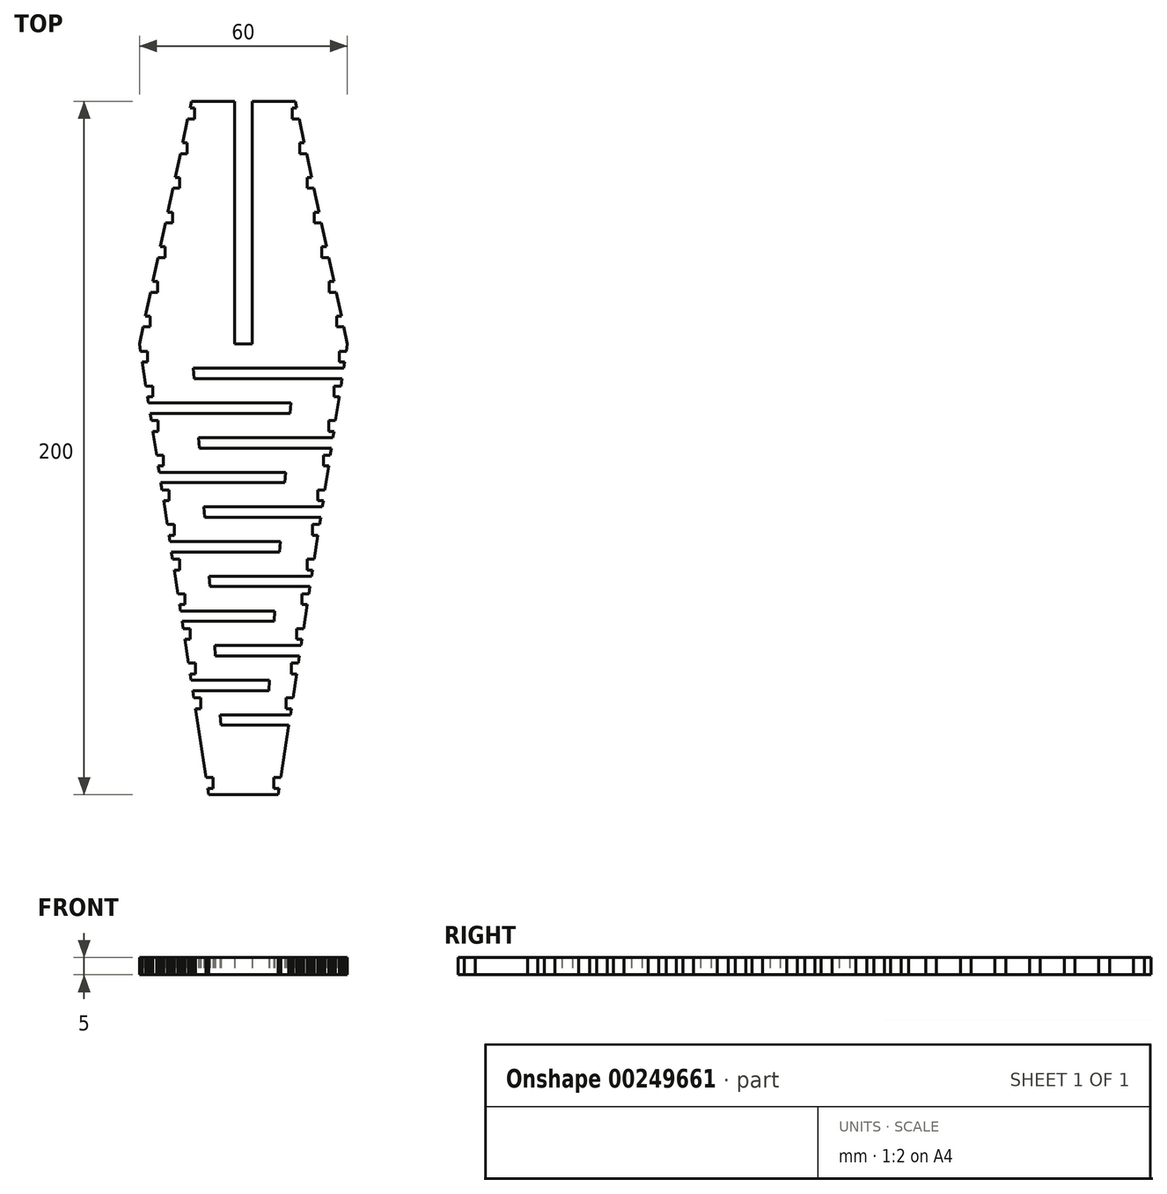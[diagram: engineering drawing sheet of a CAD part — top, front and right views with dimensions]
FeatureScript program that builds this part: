
annotation { "Feature Type Name" : "Feature", "Feature Type Description" : "" }
export const myFeature = defineFeature(function(context is Context, id is Id, definition is map)
    precondition{}
    {
        {
            var Q0;
            Q0=qCreatedBy(makeId("Top.planeOp"),FACE);
            var sketch = newSketch(context, id + "F0", { "sketchPlane" : qUnion([Q0])});
            skLineSegment(sketch, "E0", {"start": v(-15, 100) * mm, "end": v(-2.5, 100) * mm});
            skLineSegment(sketch, "E1", {"start": v(2.5, 100) * mm, "end": v(15, 100) * mm});
            skLineSegment(sketch, "E2", {"start": v(15, 100) * mm, "end": v(15.42, 98.05) * mm});
            skLineSegment(sketch, "E3", {"start": v(16.08, 94.95) * mm, "end": v(17.56, 88.05) * mm});
            skLineSegment(sketch, "E4", {"start": v(18.22, 84.95) * mm, "end": v(19.7, 78.05) * mm});
            skLineSegment(sketch, "E5", {"start": v(20.37, 74.95) * mm, "end": v(21.85, 68.05) * mm});
            skLineSegment(sketch, "E6", {"start": v(22.51, 64.95) * mm, "end": v(23.99, 58.05) * mm});
            skLineSegment(sketch, "E7", {"start": v(24.65, 54.95) * mm, "end": v(26.13, 48.05) * mm});
            skLineSegment(sketch, "E8", {"start": v(26.8, 44.95) * mm, "end": v(28.28, 38.05) * mm});
            skLineSegment(sketch, "E9", {"start": v(28.94, 34.95) * mm, "end": v(30, 30) * mm});
            skLineSegment(sketch, "E10", {"start": v(-15, 100) * mm, "end": v(-15.42, 98.05) * mm});
            skLineSegment(sketch, "E11", {"start": v(-16.08, 94.95) * mm, "end": v(-17.56, 88.05) * mm});
            skLineSegment(sketch, "E12", {"start": v(-18.22, 84.95) * mm, "end": v(-19.7, 78.05) * mm});
            skLineSegment(sketch, "E13", {"start": v(-20.37, 74.95) * mm, "end": v(-21.85, 68.05) * mm});
            skLineSegment(sketch, "E14", {"start": v(-22.51, 64.95) * mm, "end": v(-23.99, 58.05) * mm});
            skLineSegment(sketch, "E15", {"start": v(-24.65, 54.95) * mm, "end": v(-26.13, 48.05) * mm});
            skLineSegment(sketch, "E16", {"start": v(-26.8, 44.95) * mm, "end": v(-28.28, 38.05) * mm});
            skLineSegment(sketch, "E17", {"start": v(-28.94, 34.95) * mm, "end": v(-30, 30) * mm});
            skLineSegment(sketch, "E18", {"start": v(0, -100) * mm, "end": v(10, -100) * mm});
            skLineSegment(sketch, "E19", {"start": v(10, -100) * mm, "end": v(10.28, -98.2) * mm});
            skLineSegment(sketch, "E20", {"start": v(10.76, -95.1) * mm, "end": v(13.08, -80) * mm});
            skLineSegment(sketch, "E21", {"start": v(13.54, -77) * mm, "end": v(13.82, -75.2) * mm});
            skLineSegment(sketch, "E22", {"start": v(14.3, -72.1) * mm, "end": v(15.36, -65.2) * mm});
            skLineSegment(sketch, "E23", {"start": v(15.83, -62.1) * mm, "end": v(16.15, -60) * mm});
            skLineSegment(sketch, "E24", {"start": v(16.62, -57) * mm, "end": v(16.9, -55.2) * mm});
            skLineSegment(sketch, "E25", {"start": v(17.37, -52.1) * mm, "end": v(18.43, -45.2) * mm});
            skLineSegment(sketch, "E26", {"start": v(18.9, -42.1) * mm, "end": v(19.23, -40) * mm});
            skLineSegment(sketch, "E27", {"start": v(19.7, -37) * mm, "end": v(19.97, -35.2) * mm});
            skLineSegment(sketch, "E28", {"start": v(20.45, -32.1) * mm, "end": v(21.5, -25.2) * mm});
            skLineSegment(sketch, "E29", {"start": v(21.99, -22.1) * mm, "end": v(22.3, -20) * mm});
            skLineSegment(sketch, "E30", {"start": v(22.77, -17) * mm, "end": v(23.05, -15.2) * mm});
            skLineSegment(sketch, "E31", {"start": v(23.52, -12.1) * mm, "end": v(24.59, -5.2) * mm});
            skLineSegment(sketch, "E32", {"start": v(25.06, -2.1) * mm, "end": v(25.38, 0) * mm});
            skLineSegment(sketch, "E33", {"start": v(25.85, 3) * mm, "end": v(26.12, 4.8) * mm});
            skLineSegment(sketch, "E34", {"start": v(26.6, 7.9) * mm, "end": v(27.66, 14.8) * mm});
            skLineSegment(sketch, "E35", {"start": v(28.14, 17.9) * mm, "end": v(28.46, 20) * mm});
            skLineSegment(sketch, "E36", {"start": v(28.92, 23) * mm, "end": v(29.2, 24.8) * mm});
            skLineSegment(sketch, "E37", {"start": v(29.68, 27.9) * mm, "end": v(30, 30) * mm});
            skLineSegment(sketch, "E38", {"start": v(0, -100) * mm, "end": v(-10, -100) * mm});
            skLineSegment(sketch, "E39", {"start": v(-10, -100) * mm, "end": v(-10.28, -98.2) * mm});
            skLineSegment(sketch, "E40", {"start": v(-10.76, -95.1) * mm, "end": v(-13.82, -75.2) * mm});
            skLineSegment(sketch, "E41", {"start": v(-14.3, -72.1) * mm, "end": v(-14.62, -70) * mm});
            skLineSegment(sketch, "E42", {"start": v(-15.08, -67) * mm, "end": v(-15.36, -65.2) * mm});
            skLineSegment(sketch, "E43", {"start": v(-15.83, -62.1) * mm, "end": v(-16.9, -55.2) * mm});
            skLineSegment(sketch, "E44", {"start": v(-17.37, -52.1) * mm, "end": v(-17.7, -50) * mm});
            skLineSegment(sketch, "E45", {"start": v(-18.15, -47) * mm, "end": v(-18.43, -45.2) * mm});
            skLineSegment(sketch, "E46", {"start": v(-18.9, -42.1) * mm, "end": v(-19.97, -35.2) * mm});
            skLineSegment(sketch, "E47", {"start": v(-20.45, -32.1) * mm, "end": v(-20.77, -30) * mm});
            skLineSegment(sketch, "E48", {"start": v(-21.23, -27) * mm, "end": v(-21.5, -25.2) * mm});
            skLineSegment(sketch, "E49", {"start": v(-21.99, -22.1) * mm, "end": v(-23.05, -15.2) * mm});
            skLineSegment(sketch, "E50", {"start": v(-23.52, -12.1) * mm, "end": v(-23.85, -10) * mm});
            skLineSegment(sketch, "E51", {"start": v(-24.3, -7) * mm, "end": v(-24.59, -5.2) * mm});
            skLineSegment(sketch, "E52", {"start": v(-25.06, -2.1) * mm, "end": v(-26.12, 4.8) * mm});
            skLineSegment(sketch, "E53", {"start": v(-26.6, 7.9) * mm, "end": v(-26.92, 10) * mm});
            skLineSegment(sketch, "E54", {"start": v(-27.38, 13) * mm, "end": v(-27.66, 14.8) * mm});
            skLineSegment(sketch, "E55", {"start": v(-28.14, 17.9) * mm, "end": v(-29.2, 24.8) * mm});
            skLineSegment(sketch, "E56", {"start": v(-29.68, 27.9) * mm, "end": v(-30, 30) * mm});
            skLineSegment(sketch, "E57", {"start": v(-14.46, 23) * mm, "end": v(28.92, 23) * mm});
            skLineSegment(sketch, "E58", {"start": v(-14.23, 20) * mm, "end": v(28.46, 20) * mm});
            skLineSegment(sketch, "E59", {"start": v(-27.38, 13) * mm, "end": v(13.7, 13) * mm});
            skLineSegment(sketch, "E60", {"start": v(-26.92, 10) * mm, "end": v(13.46, 10) * mm});
            skLineSegment(sketch, "E61", {"start": v(-12.92, 3) * mm, "end": v(25.85, 3) * mm});
            skLineSegment(sketch, "E62", {"start": v(-12.7, 0) * mm, "end": v(25.38, 0) * mm});
            skLineSegment(sketch, "E63", {"start": v(-24.3, -7) * mm, "end": v(12.15, -7) * mm});
            skLineSegment(sketch, "E64", {"start": v(-23.85, -10) * mm, "end": v(11.92, -10) * mm});
            skLineSegment(sketch, "E65", {"start": v(-11.38, -17) * mm, "end": v(22.77, -17) * mm});
            skLineSegment(sketch, "E66", {"start": v(-11.15, -20) * mm, "end": v(22.3, -20) * mm});
            skLineSegment(sketch, "E67", {"start": v(-21.23, -27) * mm, "end": v(10.62, -27) * mm});
            skLineSegment(sketch, "E68", {"start": v(-20.77, -30) * mm, "end": v(10.38, -30) * mm});
            skLineSegment(sketch, "E69", {"start": v(-9.85, -37) * mm, "end": v(19.7, -37) * mm});
            skLineSegment(sketch, "E70", {"start": v(-9.62, -40) * mm, "end": v(19.23, -40) * mm});
            skLineSegment(sketch, "E71", {"start": v(-18.15, -47) * mm, "end": v(9.08, -47) * mm});
            skLineSegment(sketch, "E72", {"start": v(-17.7, -50) * mm, "end": v(8.85, -50) * mm});
            skLineSegment(sketch, "E73", {"start": v(-8.3, -57) * mm, "end": v(16.62, -57) * mm});
            skLineSegment(sketch, "E74", {"start": v(-8.08, -60) * mm, "end": v(16.15, -60) * mm});
            skLineSegment(sketch, "E75", {"start": v(-15.08, -67) * mm, "end": v(7.54, -67) * mm});
            skLineSegment(sketch, "E76", {"start": v(-14.62, -70) * mm, "end": v(7.3, -70) * mm});
            skLineSegment(sketch, "E77", {"start": v(-6.77, -77) * mm, "end": v(13.54, -77) * mm});
            skLineSegment(sketch, "E78", {"start": v(-6.54, -80) * mm, "end": v(13.08, -80) * mm});
            skLineSegment(sketch, "E79", {"start": v(-12.92, 3) * mm, "end": v(-12.7, 0) * mm});
            skLineSegment(sketch, "E80", {"start": v(-11.38, -17) * mm, "end": v(-11.15, -20) * mm});
            skLineSegment(sketch, "E81", {"start": v(-9.85, -37) * mm, "end": v(-9.62, -40) * mm});
            skLineSegment(sketch, "E82", {"start": v(-8.3, -57) * mm, "end": v(-8.08, -60) * mm});
            skLineSegment(sketch, "E83", {"start": v(-6.77, -77) * mm, "end": v(-6.54, -80) * mm});
            skLineSegment(sketch, "E84", {"start": v(7.54, -67) * mm, "end": v(7.3, -70) * mm});
            skLineSegment(sketch, "E85", {"start": v(9.08, -47) * mm, "end": v(8.85, -50) * mm});
            skLineSegment(sketch, "E86", {"start": v(13.7, 13) * mm, "end": v(13.46, 10) * mm});
            skLineSegment(sketch, "E87", {"start": v(12.15, -7) * mm, "end": v(11.92, -10) * mm});
            skLineSegment(sketch, "E88", {"start": v(10.62, -27) * mm, "end": v(10.38, -30) * mm});
            skLineSegment(sketch, "E89", {"start": v(-26.94, 34.95) * mm, "end": v(-26.94, 38.05) * mm});
            skLineSegment(sketch, "E90", {"start": v(-14.08, 94.95) * mm, "end": v(-14.08, 98.05) * mm});
            skLineSegment(sketch, "E91", {"start": v(-2.5, 100) * mm, "end": v(-2.5, 30) * mm});
            skLineSegment(sketch, "E92", {"start": v(-2.5, 30) * mm, "end": v(2.5, 30) * mm});
            skLineSegment(sketch, "E93", {"start": v(2.5, 30) * mm, "end": v(2.5, 100) * mm});
            skLineSegment(sketch, "E94", {"start": v(-15.42, 98.05) * mm, "end": v(-14.08, 98.05) * mm});
            skLineSegment(sketch, "E95", {"start": v(-16.08, 94.95) * mm, "end": v(-14.08, 94.95) * mm});
            skLineSegment(sketch, "E96", {"start": v(-17.56, 88.05) * mm, "end": v(-16.22, 88.05) * mm});
            skLineSegment(sketch, "E97", {"start": v(-18.22, 84.95) * mm, "end": v(-16.22, 84.95) * mm});
            skLineSegment(sketch, "E98", {"start": v(-19.7, 78.05) * mm, "end": v(-18.37, 78.05) * mm});
            skLineSegment(sketch, "E99", {"start": v(-20.37, 74.95) * mm, "end": v(-18.37, 74.95) * mm});
            skLineSegment(sketch, "E100", {"start": v(-21.85, 68.05) * mm, "end": v(-20.51, 68.05) * mm});
            skLineSegment(sketch, "E101", {"start": v(-22.51, 64.95) * mm, "end": v(-20.51, 64.95) * mm});
            skLineSegment(sketch, "E102", {"start": v(-23.99, 58.05) * mm, "end": v(-22.65, 58.05) * mm});
            skLineSegment(sketch, "E103", {"start": v(-24.65, 54.95) * mm, "end": v(-22.65, 54.95) * mm});
            skLineSegment(sketch, "E104", {"start": v(-26.13, 48.05) * mm, "end": v(-24.8, 48.05) * mm});
            skLineSegment(sketch, "E105", {"start": v(-26.8, 44.95) * mm, "end": v(-24.8, 44.95) * mm});
            skLineSegment(sketch, "E106", {"start": v(-28.28, 38.05) * mm, "end": v(-26.94, 38.05) * mm});
            skLineSegment(sketch, "E107", {"start": v(-28.94, 34.95) * mm, "end": v(-26.94, 34.95) * mm});
            skLineSegment(sketch, "E108", {"start": v(-24.8, 44.95) * mm, "end": v(-24.8, 48.05) * mm});
            skLineSegment(sketch, "E109", {"start": v(-22.65, 54.95) * mm, "end": v(-22.65, 58.05) * mm});
            skLineSegment(sketch, "E110", {"start": v(-20.51, 64.95) * mm, "end": v(-20.51, 68.05) * mm});
            skLineSegment(sketch, "E111", {"start": v(-18.37, 74.95) * mm, "end": v(-18.37, 78.05) * mm});
            skLineSegment(sketch, "E112", {"start": v(-16.22, 84.95) * mm, "end": v(-16.22, 88.05) * mm});
            skLineSegment(sketch, "E113", {"start": v(-14.23, 20) * mm, "end": v(-14.46, 23) * mm});
            skLineSegment(sketch, "E114", {"start": v(-27.68, 27.9) * mm, "end": v(-27.68, 24.8) * mm});
            skLineSegment(sketch, "E115", {"start": v(-26.14, 17.9) * mm, "end": v(-26.14, 14.8) * mm});
            skLineSegment(sketch, "E116", {"start": v(-29.68, 27.9) * mm, "end": v(-27.68, 27.9) * mm});
            skLineSegment(sketch, "E117", {"start": v(-29.2, 24.8) * mm, "end": v(-27.68, 24.8) * mm});
            skLineSegment(sketch, "E118", {"start": v(-28.14, 17.9) * mm, "end": v(-26.14, 17.9) * mm});
            skLineSegment(sketch, "E119", {"start": v(-27.66, 14.8) * mm, "end": v(-26.14, 14.8) * mm});
            skLineSegment(sketch, "E120", {"start": v(-15.83, -62.1) * mm, "end": v(-13.83, -62.1) * mm});
            skLineSegment(sketch, "E121", {"start": v(-15.36, -65.2) * mm, "end": v(-13.83, -65.2) * mm});
            skLineSegment(sketch, "E122", {"start": v(-14.3, -72.1) * mm, "end": v(-12.3, -72.1) * mm});
            skLineSegment(sketch, "E123", {"start": v(-13.82, -75.2) * mm, "end": v(-12.3, -75.2) * mm});
            skLineSegment(sketch, "E124", {"start": v(-10.76, -95.1) * mm, "end": v(-8.76, -95.1) * mm});
            skLineSegment(sketch, "E125", {"start": v(-10.28, -98.2) * mm, "end": v(-8.76, -98.2) * mm});
            skLineSegment(sketch, "E126", {"start": v(-8.76, -95.1) * mm, "end": v(-8.76, -98.2) * mm});
            skLineSegment(sketch, "E127", {"start": v(-12.3, -72.1) * mm, "end": v(-12.3, -75.2) * mm});
            skLineSegment(sketch, "E128", {"start": v(-13.83, -62.1) * mm, "end": v(-13.83, -65.2) * mm});
            skLineSegment(sketch, "E129", {"start": v(-17.37, -52.1) * mm, "end": v(-15.37, -52.1) * mm});
            skLineSegment(sketch, "E130", {"start": v(-16.9, -55.2) * mm, "end": v(-15.37, -55.2) * mm});
            skLineSegment(sketch, "E131", {"start": v(-18.9, -42.1) * mm, "end": v(-16.9, -42.1) * mm});
            skLineSegment(sketch, "E132", {"start": v(-18.43, -45.2) * mm, "end": v(-16.9, -45.2) * mm});
            skLineSegment(sketch, "E133", {"start": v(-20.45, -32.1) * mm, "end": v(-18.45, -32.1) * mm});
            skLineSegment(sketch, "E134", {"start": v(-19.97, -35.2) * mm, "end": v(-18.45, -35.2) * mm});
            skLineSegment(sketch, "E135", {"start": v(-21.99, -22.1) * mm, "end": v(-19.99, -22.1) * mm});
            skLineSegment(sketch, "E136", {"start": v(-21.5, -25.2) * mm, "end": v(-19.99, -25.2) * mm});
            skLineSegment(sketch, "E137", {"start": v(-23.52, -12.1) * mm, "end": v(-21.52, -12.1) * mm});
            skLineSegment(sketch, "E138", {"start": v(-23.05, -15.2) * mm, "end": v(-21.52, -15.2) * mm});
            skLineSegment(sketch, "E139", {"start": v(-25.06, -2.1) * mm, "end": v(-23.06, -2.1) * mm});
            skLineSegment(sketch, "E140", {"start": v(-24.59, -5.2) * mm, "end": v(-23.06, -5.2) * mm});
            skLineSegment(sketch, "E141", {"start": v(-26.6, 7.9) * mm, "end": v(-24.6, 7.9) * mm});
            skLineSegment(sketch, "E142", {"start": v(-26.12, 4.8) * mm, "end": v(-24.6, 4.8) * mm});
            skLineSegment(sketch, "E143", {"start": v(-15.37, -52.1) * mm, "end": v(-15.37, -55.2) * mm});
            skLineSegment(sketch, "E144", {"start": v(-16.9, -42.1) * mm, "end": v(-16.9, -45.2) * mm});
            skLineSegment(sketch, "E145", {"start": v(-18.45, -32.1) * mm, "end": v(-18.45, -35.2) * mm});
            skLineSegment(sketch, "E146", {"start": v(-19.99, -22.1) * mm, "end": v(-19.99, -25.2) * mm});
            skLineSegment(sketch, "E147", {"start": v(-21.52, -12.1) * mm, "end": v(-21.52, -15.2) * mm});
            skLineSegment(sketch, "E148", {"start": v(-23.06, -2.1) * mm, "end": v(-23.06, -5.2) * mm});
            skLineSegment(sketch, "E149", {"start": v(-24.6, 7.9) * mm, "end": v(-24.6, 4.8) * mm});
            skLineSegment(sketch, "E150", {"start": v(15.08, -67) * mm, "end": v(15.36, -65.2) * mm});
            skLineSegment(sketch, "E151", {"start": v(15.83, -62.1) * mm, "end": v(16.9, -55.2) * mm});
            skLineSegment(sketch, "E152", {"start": v(17.37, -52.1) * mm, "end": v(17.7, -50) * mm});
            skLineSegment(sketch, "E153", {"start": v(21.23, -27) * mm, "end": v(21.5, -25.2) * mm});
            skLineSegment(sketch, "E154", {"start": v(21.99, -22.1) * mm, "end": v(23.05, -15.2) * mm});
            skLineSegment(sketch, "E155", {"start": v(23.52, -12.1) * mm, "end": v(23.85, -10) * mm});
            skLineSegment(sketch, "E156", {"start": v(24.3, -7) * mm, "end": v(24.59, -5.2) * mm});
            skLineSegment(sketch, "E157", {"start": v(25.06, -2.1) * mm, "end": v(26.12, 4.8) * mm});
            skLineSegment(sketch, "E158", {"start": v(26.6, 7.9) * mm, "end": v(26.92, 10) * mm});
            skLineSegment(sketch, "E159", {"start": v(27.38, 13) * mm, "end": v(27.66, 14.8) * mm});
            skLineSegment(sketch, "E160", {"start": v(28.14, 17.9) * mm, "end": v(29.2, 24.8) * mm});
            skLineSegment(sketch, "E161", {"start": v(26.94, 34.95) * mm, "end": v(26.94, 38.05) * mm});
            skLineSegment(sketch, "E162", {"start": v(14.08, 94.95) * mm, "end": v(14.08, 98.05) * mm});
            skLineSegment(sketch, "E163", {"start": v(15.42, 98.05) * mm, "end": v(14.08, 98.05) * mm});
            skLineSegment(sketch, "E164", {"start": v(16.08, 94.95) * mm, "end": v(14.08, 94.95) * mm});
            skLineSegment(sketch, "E165", {"start": v(17.56, 88.05) * mm, "end": v(16.22, 88.05) * mm});
            skLineSegment(sketch, "E166", {"start": v(18.22, 84.95) * mm, "end": v(16.22, 84.95) * mm});
            skLineSegment(sketch, "E167", {"start": v(19.7, 78.05) * mm, "end": v(18.37, 78.05) * mm});
            skLineSegment(sketch, "E168", {"start": v(20.37, 74.95) * mm, "end": v(18.37, 74.95) * mm});
            skLineSegment(sketch, "E169", {"start": v(21.85, 68.05) * mm, "end": v(20.5, 68.05) * mm});
            skLineSegment(sketch, "E170", {"start": v(22.51, 64.95) * mm, "end": v(20.5, 64.95) * mm});
            skLineSegment(sketch, "E171", {"start": v(23.99, 58.05) * mm, "end": v(22.65, 58.05) * mm});
            skLineSegment(sketch, "E172", {"start": v(24.65, 54.95) * mm, "end": v(22.65, 54.95) * mm});
            skLineSegment(sketch, "E173", {"start": v(26.13, 48.05) * mm, "end": v(24.8, 48.05) * mm});
            skLineSegment(sketch, "E174", {"start": v(26.8, 44.95) * mm, "end": v(24.8, 44.95) * mm});
            skLineSegment(sketch, "E175", {"start": v(28.28, 38.05) * mm, "end": v(26.94, 38.05) * mm});
            skLineSegment(sketch, "E176", {"start": v(28.94, 34.95) * mm, "end": v(26.94, 34.95) * mm});
            skLineSegment(sketch, "E177", {"start": v(24.8, 44.95) * mm, "end": v(24.8, 48.05) * mm});
            skLineSegment(sketch, "E178", {"start": v(22.65, 54.95) * mm, "end": v(22.65, 58.05) * mm});
            skLineSegment(sketch, "E179", {"start": v(20.5, 64.95) * mm, "end": v(20.5, 68.05) * mm});
            skLineSegment(sketch, "E180", {"start": v(18.37, 74.95) * mm, "end": v(18.37, 78.05) * mm});
            skLineSegment(sketch, "E181", {"start": v(16.22, 84.95) * mm, "end": v(16.22, 88.05) * mm});
            skLineSegment(sketch, "E182", {"start": v(27.68, 27.9) * mm, "end": v(27.68, 24.8) * mm});
            skLineSegment(sketch, "E183", {"start": v(26.14, 17.9) * mm, "end": v(26.14, 14.8) * mm});
            skLineSegment(sketch, "E184", {"start": v(29.68, 27.9) * mm, "end": v(27.68, 27.9) * mm});
            skLineSegment(sketch, "E185", {"start": v(29.2, 24.8) * mm, "end": v(27.68, 24.8) * mm});
            skLineSegment(sketch, "E186", {"start": v(28.14, 17.9) * mm, "end": v(26.14, 17.9) * mm});
            skLineSegment(sketch, "E187", {"start": v(27.66, 14.8) * mm, "end": v(26.14, 14.8) * mm});
            skLineSegment(sketch, "E188", {"start": v(15.83, -62.1) * mm, "end": v(13.83, -62.1) * mm});
            skLineSegment(sketch, "E189", {"start": v(15.36, -65.2) * mm, "end": v(13.83, -65.2) * mm});
            skLineSegment(sketch, "E190", {"start": v(14.3, -72.1) * mm, "end": v(12.3, -72.1) * mm});
            skLineSegment(sketch, "E191", {"start": v(13.82, -75.2) * mm, "end": v(12.3, -75.2) * mm});
            skLineSegment(sketch, "E192", {"start": v(10.76, -95.1) * mm, "end": v(8.76, -95.1) * mm});
            skLineSegment(sketch, "E193", {"start": v(10.28, -98.2) * mm, "end": v(8.76, -98.2) * mm});
            skLineSegment(sketch, "E194", {"start": v(8.76, -95.1) * mm, "end": v(8.76, -98.2) * mm});
            skLineSegment(sketch, "E195", {"start": v(12.3, -72.1) * mm, "end": v(12.3, -75.2) * mm});
            skLineSegment(sketch, "E196", {"start": v(13.83, -62.1) * mm, "end": v(13.83, -65.2) * mm});
            skLineSegment(sketch, "E197", {"start": v(17.37, -52.1) * mm, "end": v(15.37, -52.1) * mm});
            skLineSegment(sketch, "E198", {"start": v(16.9, -55.2) * mm, "end": v(15.37, -55.2) * mm});
            skLineSegment(sketch, "E199", {"start": v(18.9, -42.1) * mm, "end": v(16.9, -42.1) * mm});
            skLineSegment(sketch, "E200", {"start": v(18.43, -45.2) * mm, "end": v(16.9, -45.2) * mm});
            skLineSegment(sketch, "E201", {"start": v(20.45, -32.1) * mm, "end": v(18.45, -32.1) * mm});
            skLineSegment(sketch, "E202", {"start": v(19.97, -35.2) * mm, "end": v(18.45, -35.2) * mm});
            skLineSegment(sketch, "E203", {"start": v(21.99, -22.1) * mm, "end": v(19.99, -22.1) * mm});
            skLineSegment(sketch, "E204", {"start": v(21.5, -25.2) * mm, "end": v(19.99, -25.2) * mm});
            skLineSegment(sketch, "E205", {"start": v(23.52, -12.1) * mm, "end": v(21.52, -12.1) * mm});
            skLineSegment(sketch, "E206", {"start": v(23.05, -15.2) * mm, "end": v(21.52, -15.2) * mm});
            skLineSegment(sketch, "E207", {"start": v(25.06, -2.1) * mm, "end": v(23.06, -2.1) * mm});
            skLineSegment(sketch, "E208", {"start": v(24.59, -5.2) * mm, "end": v(23.06, -5.2) * mm});
            skLineSegment(sketch, "E209", {"start": v(26.6, 7.9) * mm, "end": v(24.6, 7.9) * mm});
            skLineSegment(sketch, "E210", {"start": v(26.12, 4.8) * mm, "end": v(24.6, 4.8) * mm});
            skLineSegment(sketch, "E211", {"start": v(15.37, -52.1) * mm, "end": v(15.37, -55.2) * mm});
            skLineSegment(sketch, "E212", {"start": v(16.9, -42.1) * mm, "end": v(16.9, -45.2) * mm});
            skLineSegment(sketch, "E213", {"start": v(18.45, -32.1) * mm, "end": v(18.45, -35.2) * mm});
            skLineSegment(sketch, "E214", {"start": v(19.99, -22.1) * mm, "end": v(19.99, -25.2) * mm});
            skLineSegment(sketch, "E215", {"start": v(21.52, -12.1) * mm, "end": v(21.52, -15.2) * mm});
            skLineSegment(sketch, "E216", {"start": v(23.06, -2.1) * mm, "end": v(23.06, -5.2) * mm});
            skLineSegment(sketch, "E217", {"start": v(24.6, 7.9) * mm, "end": v(24.6, 4.8) * mm});
            skSolve(sketch);
        }
        {
            var Q0;
            Q0=makeQuery(id+"F0.imprint","IMPRINT",FACE,{"disambiguationData":[TD([[makeQuery(id+"F0.imprint","IMPRINT",EDGE,{"derivedFrom":sQuery(id+"F0.wireOp",EDGE,"E0")}),-1.0]])]});
            extrude(context, id + "F1", {"entities" : qUnion([Q0]), "depth" : 5 * mm});
        }
    });
